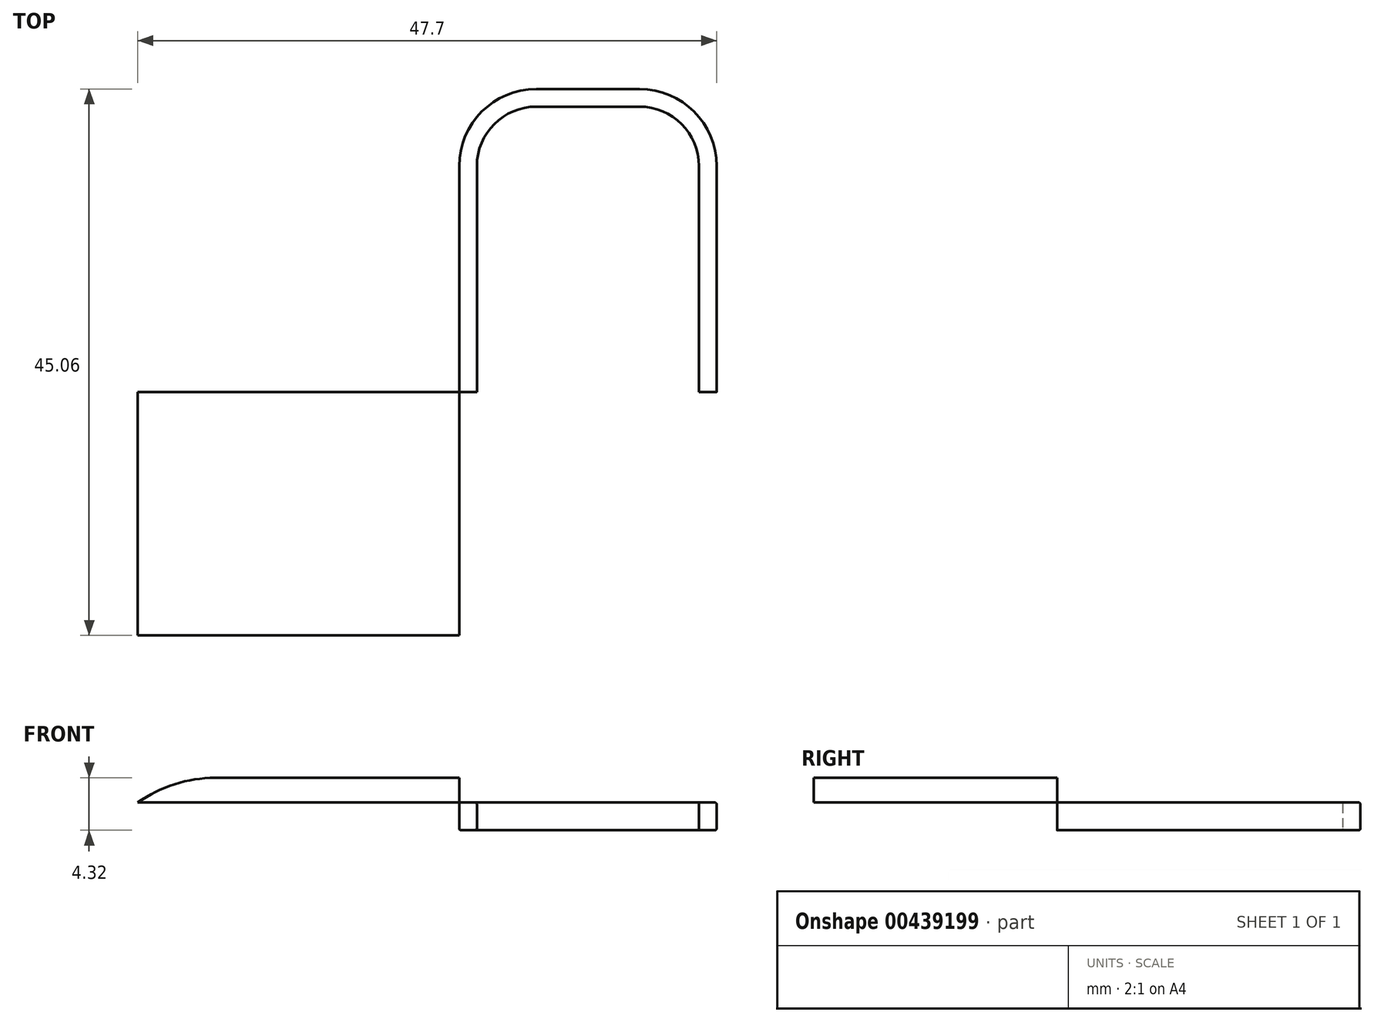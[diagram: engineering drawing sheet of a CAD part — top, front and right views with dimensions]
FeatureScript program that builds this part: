
annotation { "Feature Type Name" : "Feature", "Feature Type Description" : "" }
export const myFeature = defineFeature(function(context is Context, id is Id, definition is map)
    precondition{}
    {
        {
            var Q0;
            Q0=qCreatedBy(makeId("Top.planeOp"),FACE);
            var sketch = newSketch(context, id + "F0", { "sketchPlane" : qUnion([Q0])});
            skLineSegment(sketch, "E0", {"start": v(0, 0) * mm, "end": v(0, 18.65) * mm});
            skLineSegment(sketch, "E1", {"start": v(6.35, 25) * mm, "end": v(14.86, 25) * mm});
            skLineSegment(sketch, "E2", {"start": v(21.2, 18.65) * mm, "end": v(21.2, 0) * mm});
            skPoint(sketch, "E3.visualSharp", {"position": v(0, 25) * mm});
            skArc(sketch, "E3.filletArc", {"start": v(6.35, 25) * mm, "mid": v(1.86, 23.14) * mm, "end": v(0, 18.65) * mm});
            skPoint(sketch, "E4.visualSharp", {"position": v(21.2, 25) * mm});
            skArc(sketch, "E4.filletArc", {"start": v(21.2, 18.65) * mm, "mid": v(19.35, 23.14) * mm, "end": v(14.86, 25) * mm});
            skSolve(sketch);
        }
        {
            var Q0;
            Q0=qCreatedBy(makeId("Front.planeOp"),FACE);
            var sketch = newSketch(context, id + "F1", { "sketchPlane" : qUnion([Q0])});
            skLineSegment(sketch, "E5.bottom", {"start": v(0.15, 0) * mm, "end": v(1.3, 0) * mm});
            skLineSegment(sketch, "E5.top", {"start": v(0.15, -2.3) * mm, "end": v(1.3, -2.3) * mm});
            skLineSegment(sketch, "E5.left", {"start": v(0, -0.15) * mm, "end": v(0, -2.15) * mm});
            skLineSegment(sketch, "E5.right", {"start": v(1.45, -0.15) * mm, "end": v(1.45, -2.15) * mm});
            skPoint(sketch, "E6.visualSharp", {"position": v(0, 0) * mm});
            skArc(sketch, "E6.filletArc", {"start": v(0.15, 0) * mm, "mid": v(0.04, -0.04) * mm, "end": v(0, -0.15) * mm});
            skPoint(sketch, "E7.visualSharp", {"position": v(1.45, 0) * mm});
            skArc(sketch, "E7.filletArc", {"start": v(1.45, -0.15) * mm, "mid": v(1.4, -0.04) * mm, "end": v(1.3, 0) * mm});
            skPoint(sketch, "E8.visualSharp", {"position": v(1.45, -2.3) * mm});
            skArc(sketch, "E8.filletArc", {"start": v(1.3, -2.3) * mm, "mid": v(1.4, -2.25) * mm, "end": v(1.45, -2.15) * mm});
            skPoint(sketch, "E9.visualSharp", {"position": v(0, -2.3) * mm});
            skArc(sketch, "E9.filletArc", {"start": v(0, -2.15) * mm, "mid": v(0.04, -2.25) * mm, "end": v(0.15, -2.3) * mm});
            skSolve(sketch);
        }
        {
            var Q0;
            Q0=qCreatedBy(makeId("Top.planeOp"),FACE);
            var sketch = newSketch(context, id + "F2", { "sketchPlane" : qUnion([Q0])});
            skLineSegment(sketch, "E10.bottom", {"start": v(0, -20.06) * mm, "end": v(-26.5, -20.06) * mm});
            skLineSegment(sketch, "E10.top", {"start": v(0, 0) * mm, "end": v(-26.5, 0) * mm});
            skLineSegment(sketch, "E10.left", {"start": v(0, -20.06) * mm, "end": v(0, 0) * mm});
            skLineSegment(sketch, "E10.right", {"start": v(-26.5, -20.06) * mm, "end": v(-26.5, 0) * mm});
            skSolve(sketch);
        }
        {
            var Q0;
            Q0 = qSketchRegion(id + "F2", true);
            extrude(context, id + "F3", {"entities" : qUnion([Q0]), "depth" : 2.03 * mm});
        }
        {
            var Q0;
            Q0=makeQuery(id+"F3.opExtrude","CAP_EDGE",EDGE,{"disambiguationData":[OSD([sQuery(id+"F2.wireOp",EDGE,"E10.right")])],"isStart":false});
            fillet(context, id + "F4", {"entities" : qUnion([Q0]), "radius" : 11.04 * mm, "tangentPropagation" : true, "allowEdgeOverflow" : false});
        }
        {
            var Q0;
            Q0=makeQuery(id+"F1.imprint","IMPRINT",FACE,{"disambiguationData":[TD([[makeQuery(id+"F1.imprint","IMPRINT",EDGE,{"derivedFrom":sQuery(id+"F1.wireOp",EDGE,"E5.bottom")}),-1.0]])]});
            var Q1;
            Q1=sQuery(id+"F0.wireOp",EDGE,"E0");
            var Q2;
            Q2=sQuery(id+"F0.wireOp",EDGE,"E1");
            var Q3;
            Q3=sQuery(id+"F0.wireOp",EDGE,"E2");
            var Q4;
            Q4=sQuery(id+"F0.wireOp",EDGE,"E3.filletArc");
            var Q5;
            Q5=sQuery(id+"F0.wireOp",EDGE,"E4.filletArc");
            sweep(context, id + "F5", {"profiles" : qUnion([Q0]), "path" : qUnion([Q1, Q2, Q3, Q4, Q5])});
        }
    });
